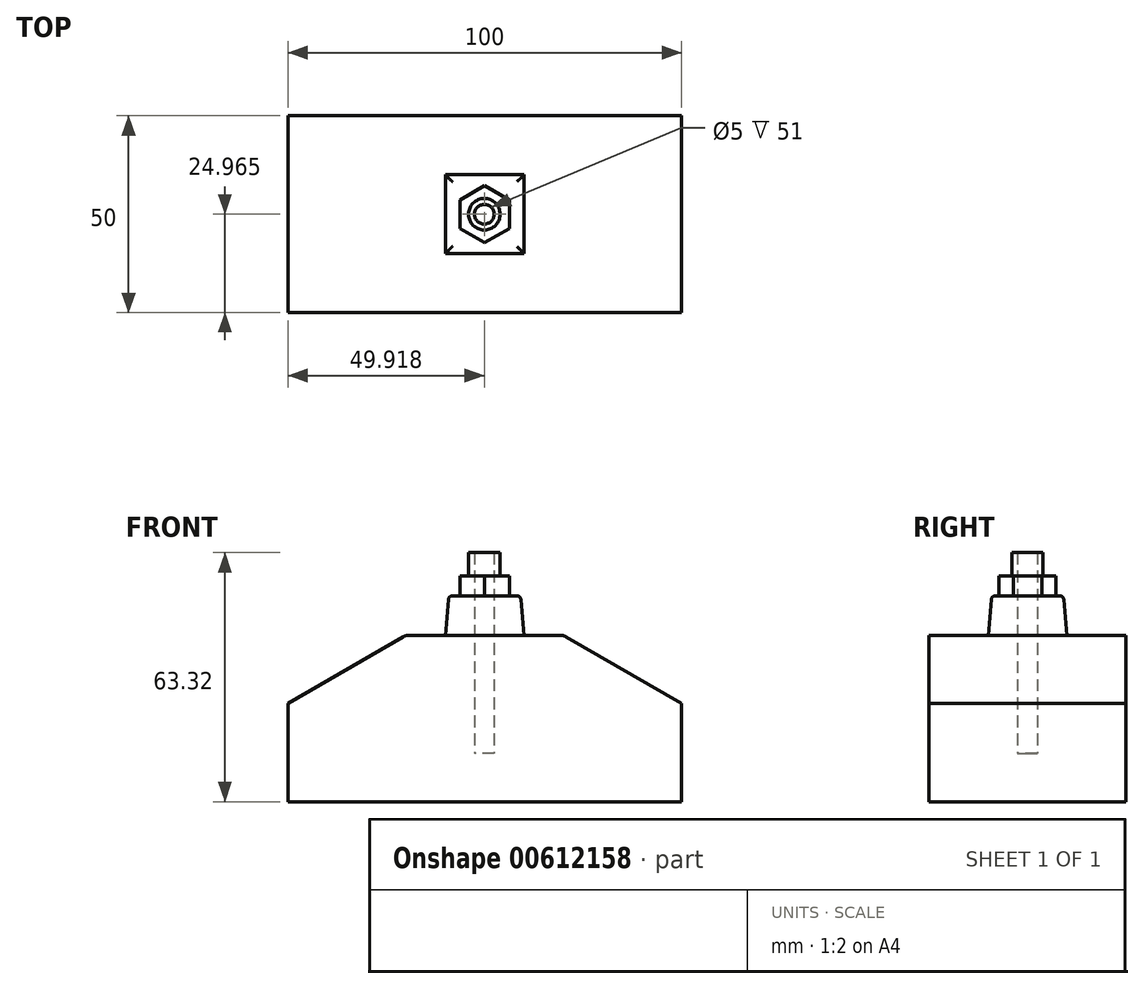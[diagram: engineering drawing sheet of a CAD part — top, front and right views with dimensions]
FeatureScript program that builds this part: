
annotation { "Feature Type Name" : "Feature", "Feature Type Description" : "" }
export const myFeature = defineFeature(function(context is Context, id is Id, definition is map)
    precondition{}
    {
        {
            var Q0;
            Q0=qCreatedBy(makeId("Front.planeOp"),FACE);
            var sketch = newSketch(context, id + "F0", { "sketchPlane" : qUnion([Q0])});
            skLineSegment(sketch, "E0", {"start": v(-50, 0) * mm, "end": v(50, 0) * mm});
            skLineSegment(sketch, "E1", {"start": v(50, 0) * mm, "end": v(50, 25) * mm});
            skLineSegment(sketch, "E2", {"start": v(50, 25) * mm, "end": v(20, 42.32) * mm});
            skLineSegment(sketch, "E3", {"start": v(20, 42.32) * mm, "end": v(-20, 42.32) * mm});
            skLineSegment(sketch, "E4", {"start": v(-20, 42.32) * mm, "end": v(-50, 25) * mm});
            skLineSegment(sketch, "E5", {"start": v(-50, 25) * mm, "end": v(-50, 0) * mm});
            skSolve(sketch);
        }
        {
            var Q0;
            Q0=makeQuery(id+"F0.imprint","IMPRINT",FACE,{"disambiguationData":[TD([[makeQuery(id+"F0.imprint","IMPRINT",EDGE,{"derivedFrom":sQuery(id+"F0.wireOp",EDGE,"E0")}),1.0]])]});
            extrude(context, id + "F1", {"entities" : qUnion([Q0]), "endBound" : BoundingType.SYMMETRIC, "depth" : 50 * mm, "offsetDistance" : 25 * mm});
        }
        {
            var Q0;
            Q0=makeQuery(id+"F1.opExtrude","SWEPT_FACE",FACE,{"disambiguationData":[OSD([sQuery(id+"F0.wireOp",EDGE,"E3")])]});
            var sketch = newSketch(context, id + "F2", { "sketchPlane" : qUnion([Q0])});
            skLineSegment(sketch, "E6.bottom", {"start": v(10, -10) * mm, "end": v(-10, -10) * mm});
            skLineSegment(sketch, "E6.top", {"start": v(10, 10) * mm, "end": v(-10, 10) * mm});
            skLineSegment(sketch, "E6.left", {"start": v(10, -10) * mm, "end": v(10, 10) * mm});
            skLineSegment(sketch, "E6.right", {"start": v(-10, -10) * mm, "end": v(-10, 10) * mm});
            skPoint(sketch, "E6.middle", {"position": v(0, 0) * mm});
            skSolve(sketch);
        }
        {
            var Q0;
            Q0=makeQuery(id+"F2.imprint","IMPRINT",FACE,{"disambiguationData":[TD([[makeQuery(id+"F2.imprint","IMPRINT",EDGE,{"derivedFrom":sQuery(id+"F2.wireOp",EDGE,"E6.bottom")}),-1.0]])]});
            extrude(context, id + "F3", {"entities" : qUnion([Q0]), "operationType" : NewBodyOperationType.ADD, "depth" : 10 * mm, "offsetDistance" : 25 * mm, "hasDraft" : true, "draftAngle" : 5 * degree, "draftPullDirection" : true});
        }
        {
            var Q0;
            Q0=makeQuery(id+"F3.opExtrude","CAP_FACE",FACE,{"disambiguationData":[OSD([sQuery(id+"F2.wireOp",EDGE,"E6.bottom"),sQuery(id+"F2.wireOp",EDGE,"E6.top"),sQuery(id+"F2.wireOp",EDGE,"E6.left"),sQuery(id+"F2.wireOp",EDGE,"E6.right")])],"isStart":false});
            var sketch = newSketch(context, id + "F4", { "sketchPlane" : qUnion([Q0])});
            skCircle(sketch, "E7.cCircle", {"center": v(0, 0) * mm, "radius": 7.25 * mm, "construction": true});
            skLineSegment(sketch, "E7.0", {"start": v(0, -7.25) * mm, "end": v(-6.28, -3.63) * mm});
            skLineSegment(sketch, "E7.1", {"start": v(-6.28, -3.63) * mm, "end": v(-6.28, 3.62) * mm});
            skLineSegment(sketch, "E7.2", {"start": v(-6.28, 3.62) * mm, "end": v(0, 7.25) * mm});
            skLineSegment(sketch, "E7.3", {"start": v(0, 7.25) * mm, "end": v(6.28, 3.63) * mm});
            skLineSegment(sketch, "E7.4", {"start": v(6.28, 3.63) * mm, "end": v(6.28, -3.62) * mm});
            skLineSegment(sketch, "E7.5", {"start": v(6.28, -3.62) * mm, "end": v(0, -7.25) * mm});
            skSolve(sketch);
        }
        {
            var Q0;
            Q0=makeQuery(id+"F4.imprint","IMPRINT",FACE,{"disambiguationData":[TD([[makeQuery(id+"F4.imprint","IMPRINT",EDGE,{"derivedFrom":sQuery(id+"F4.wireOp",EDGE,"E7.0")}),-1.0]])]});
            extrude(context, id + "F5", {"entities" : qUnion([Q0]), "operationType" : NewBodyOperationType.ADD, "depth" : 5 * mm, "offsetDistance" : 25 * mm});
        }
        {
            var Q0;
            Q0=makeQuery(id+"F5.opExtrude","CAP_FACE",FACE,{"disambiguationData":[OSD([sQuery(id+"F4.wireOp",EDGE,"E7.0"),sQuery(id+"F4.wireOp",EDGE,"E7.1"),sQuery(id+"F4.wireOp",EDGE,"E7.2"),sQuery(id+"F4.wireOp",EDGE,"E7.3"),sQuery(id+"F4.wireOp",EDGE,"E7.4"),sQuery(id+"F4.wireOp",EDGE,"E7.5")])],"isStart":false});
            var sketch = newSketch(context, id + "F6", { "sketchPlane" : qUnion([Q0])});
            skCircle(sketch, "E8", {"center": v(-0.08, -0.04) * mm, "radius": 4 * mm});
            skPoint(sketch, "E8.first.point", {"position": v(-4.08, 0) * mm});
            skPoint(sketch, "E8.second.point", {"position": v(3.92, 0) * mm});
            skPoint(sketch, "E8.third.point", {"position": v(0.42, -4) * mm});
            skCircle(sketch, "E9.0", {"center": v(-0.08, -0.04) * mm, "radius": 2.5 * mm});
            skSolve(sketch);
        }
        {
            var Q0;
            Q0=makeQuery(id+"F6.imprint","IMPRINT",FACE,{"disambiguationData":[TD([[makeQuery(id+"F6.imprint","IMPRINT",EDGE,{"derivedFrom":sQuery(id+"F6.wireOp",EDGE,"E8")}),1.0]])]});
            extrude(context, id + "F7", {"entities" : qUnion([Q0]), "operationType" : NewBodyOperationType.ADD, "depth" : 6 * mm, "offsetDistance" : 25 * mm});
        }
        {
            var Q0;
            Q0=makeQuery(id+"F7.boolean.opBoolean","SPLIT",FACE,{"disambiguationData":[TD([makeQuery(id+"F7.opExtrude","SWEPT_FACE",FACE,{"disambiguationData":[OSD([sQuery(id+"F6.wireOp",EDGE,"E9.0")])]})])],"derivedFrom":makeQuery(id+"F5.opExtrude","CAP_FACE",FACE,{"disambiguationData":[OSD([sQuery(id+"F4.wireOp",EDGE,"E7.0"),sQuery(id+"F4.wireOp",EDGE,"E7.1"),sQuery(id+"F4.wireOp",EDGE,"E7.2"),sQuery(id+"F4.wireOp",EDGE,"E7.3"),sQuery(id+"F4.wireOp",EDGE,"E7.4"),sQuery(id+"F4.wireOp",EDGE,"E7.5")])],"isStart":false})});
            extrude(context, id + "F8", {"entities" : qUnion([Q0]), "operationType" : NewBodyOperationType.REMOVE, "oppositeDirection" : true, "depth" : 45 * mm, "offsetDistance" : 25 * mm});
        }
        {
            var Q0;
            Q0=makeQuery(id+"F3.opExtrude","CAP_EDGE",EDGE,{"disambiguationData":[OSD([sQuery(id+"F2.wireOp",EDGE,"E6.bottom")])],"isStart":false});
            var Q1;
            Q1=makeQuery(id+"F3.opExtrude","CAP_EDGE",EDGE,{"disambiguationData":[OSD([sQuery(id+"F2.wireOp",EDGE,"E6.right")])],"isStart":false});
            var Q2;
            Q2=makeQuery(id+"F3.opExtrude","CAP_EDGE",EDGE,{"disambiguationData":[OSD([sQuery(id+"F2.wireOp",EDGE,"E6.left")])],"isStart":false});
            var Q3;
            Q3=makeQuery(id+"F3.opExtrude","CAP_EDGE",EDGE,{"disambiguationData":[OSD([sQuery(id+"F2.wireOp",EDGE,"E6.top")])],"isStart":false});
            var Q4;
            Q4=makeQuery(id+"F7.opExtrude","CAP_EDGE",EDGE,{"disambiguationData":[OSD([sQuery(id+"F6.wireOp",EDGE,"E8")])],"isStart":true});
            fillet(context, id + "F9", {"entities" : qUnion([Q0, Q1, Q2, Q3, Q4]), "radius" : 1 * mm, "tangentPropagation" : true, "allowEdgeOverflow" : false});
        }
        {
            var Q0;
            Q0=makeQuery(id+"F1.opExtrude","SWEPT_EDGE",EDGE,{"disambiguationData":[OSD([sQuery(id+"F0.wireOp",EDGE,"E3"),sQuery(id+"F0.wireOp",EDGE,"E4")])]});
            var Q1;
            Q1=makeQuery(id+"F1.opExtrude","SWEPT_EDGE",EDGE,{"disambiguationData":[OSD([sQuery(id+"F0.wireOp",EDGE,"E2"),sQuery(id+"F0.wireOp",EDGE,"E3")])]});
            fillet(context, id + "F10", {"entities" : qUnion([Q0, Q1]), "radius" : 3 * mm, "tangentPropagation" : true, "allowEdgeOverflow" : false});
        }
    });
